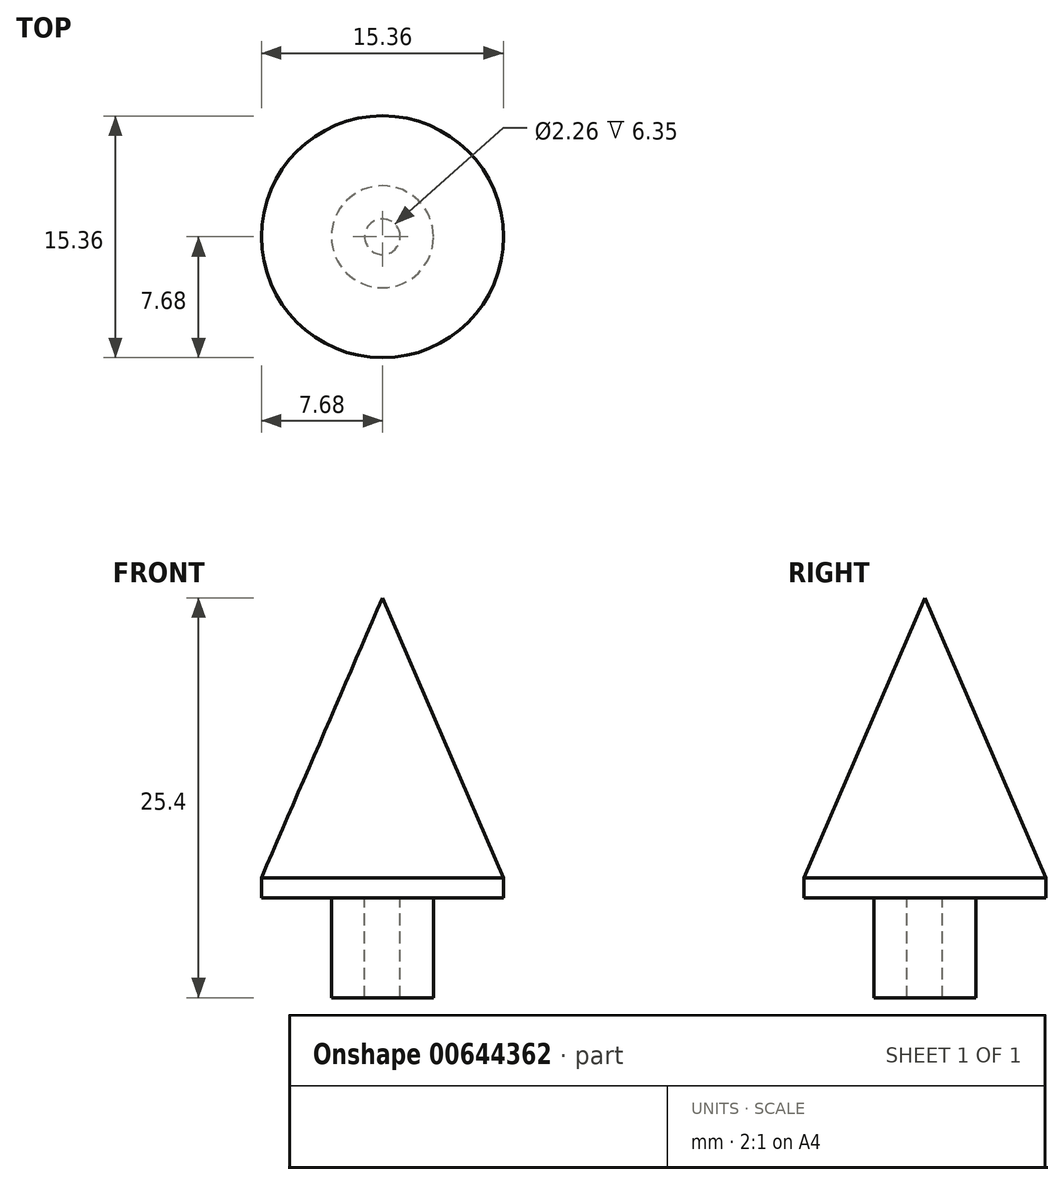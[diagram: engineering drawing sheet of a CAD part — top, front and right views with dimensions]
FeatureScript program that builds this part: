
annotation { "Feature Type Name" : "Feature", "Feature Type Description" : "" }
export const myFeature = defineFeature(function(context is Context, id is Id, definition is map)
    precondition{}
    {
        {
            var Q0;
            Q0=qCreatedBy(makeId("Front.planeOp"),FACE);
            var sketch = newSketch(context, id + "F0", { "sketchPlane" : qUnion([Q0])});
            skLineSegment(sketch, "E0", {"start": v(-7.68, 0) * mm, "end": v(-3.24, 0) * mm});
            skLineSegment(sketch, "E1", {"start": v(-3.24, 0) * mm, "end": v(-3.24, -6.35) * mm});
            skLineSegment(sketch, "E2", {"start": v(-3.24, -6.35) * mm, "end": v(0, -6.35) * mm});
            skLineSegment(sketch, "E3", {"start": v(0, -6.35) * mm, "end": v(0, 19.05) * mm});
            skLineSegment(sketch, "E4", {"start": v(-7.68, 0) * mm, "end": v(-7.68, 1.27) * mm});
            skLineSegment(sketch, "E5", {"start": v(-7.68, 1.27) * mm, "end": v(0, 19.05) * mm});
            skSolve(sketch);
        }
        {
            var Q0;
            Q0=makeQuery(id+"F0.imprint","IMPRINT",FACE,{"disambiguationData":[TD([[makeQuery(id+"F0.imprint","IMPRINT",EDGE,{"derivedFrom":sQuery(id+"F0.wireOp",EDGE,"E0")}),1.0]])]});
            var Q1;
            Q1=sQuery(id+"F0.wireOp",EDGE,"E3");
            revolve(context, id + "F1", {"entities" : qUnion([Q0]), "axis" : qUnion([Q1]), "revolveType" : RevolveType.FULL});
        }
        {
            var Q0;
            Q0=qCreatedBy(makeId("Top.planeOp"),FACE);
            var sketch = newSketch(context, id + "F2", { "sketchPlane" : qUnion([Q0])});
            skPoint(sketch, "E6", {"position": v(0, 0) * mm});
            skSolve(sketch);
        }
        {
            var Q0;
            Q0=sQuery(id+"F2.wireOp",VERTEX,"E6");
            var Q1;
            Q1=makeQuery(id+"F1.opRevolve","SWEPT_BODY",BODY,{"disambiguationData":[OSD([sQuery(id+"F0.wireOp",EDGE,"0sjXL8Im-2f2s-KyzP-CCuE-DjZiIa729Wi6"),sQuery(id+"F0.wireOp",EDGE,"E0"),sQuery(id+"F0.wireOp",EDGE,"E1"),sQuery(id+"F0.wireOp",EDGE,"E2"),sQuery(id+"F0.wireOp",EDGE,"E3")])]});
            hole(context, id + "F3", {"style" : HoleStyle.SIMPLE, "endStyle" : HoleEndStyle.THROUGH, "standardTappedOrClearance" : lookupTablePath({ "standard" : "ANSI", "engagement" : "75%", "pitch" : "40 tpi", "size" : "#4", "type" : "Tapped" }), "standardBlindInLast" : lookupTablePath({ "standard" : "ANSI", "engagement" : "75%", "pitch" : "40 tpi", "size" : "#4", "type" : "Tapped" }), "holeDiameter" : 2.26 * mm, "majorDiameter" : 2.84 * mm, "showTappedDepth" : true, "tappedDepth" : 4.57 * mm, "tapClearance" : 3, "locations" : qUnion([Q0]), "scope" : qUnion([Q1])});
        }
    });
